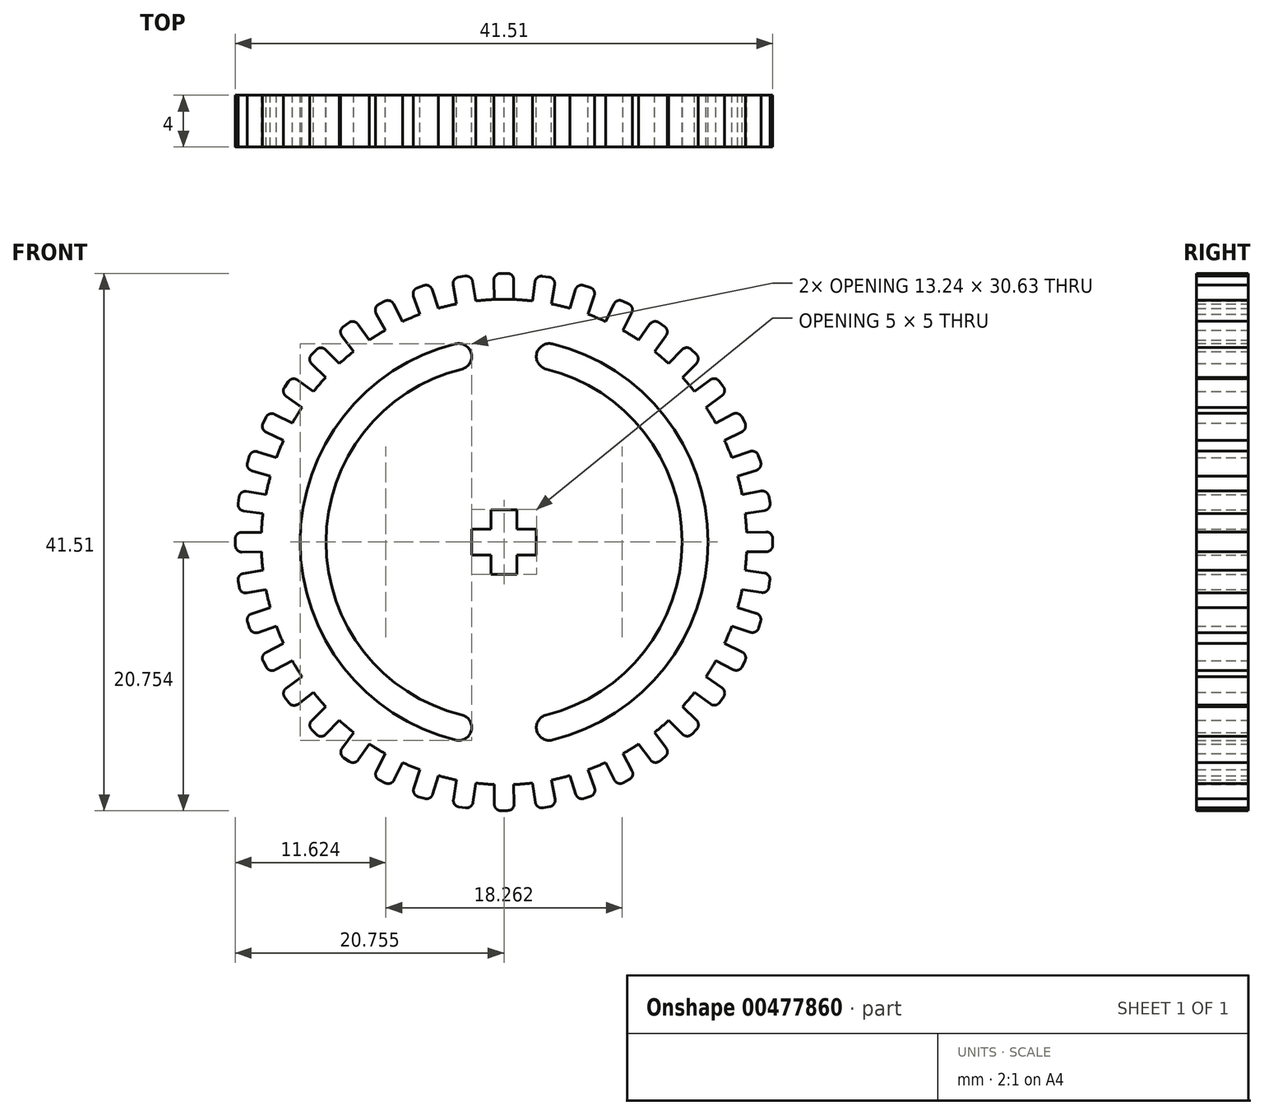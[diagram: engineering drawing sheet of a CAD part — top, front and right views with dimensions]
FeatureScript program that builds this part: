
annotation { "Feature Type Name" : "Feature", "Feature Type Description" : "" }
export const myFeature = defineFeature(function(context is Context, id is Id, definition is map)
    precondition{}
    {
        {
            var Q0;
            Q0=qCreatedBy(makeId("Front.planeOp"),FACE);
            var sketch = newSketch(context, id + "F0", { "sketchPlane" : qUnion([Q0])});
            skCircle(sketch, "E0", {"center": v(-49.28, 19.92) * mm, "radius": 18.75 * mm});
            skLineSegment(sketch, "E1.MirrorCS", {"start": v(-50.28, 22.42) * mm, "end": v(-50.28, 20.92) * mm});
            skLineSegment(sketch, "E2.MirrorCS", {"start": v(-50.28, 20.92) * mm, "end": v(-51.78, 20.92) * mm});
            skArc(sketch, "E3", {"start": v(-46.78, 6.4) * mm, "mid": v(-35.53, 19.92) * mm, "end": v(-46.78, 33.44) * mm});
            skArc(sketch, "E4", {"start": v(-46.78, 4.37) * mm, "mid": v(-33.53, 19.92) * mm, "end": v(-46.78, 35.47) * mm});
            skLineSegment(sketch, "E5", {"start": v(-51.78, 33.44) * mm, "end": v(-51.78, 35.47) * mm});
            skLineSegment(sketch, "E6", {"start": v(-46.78, 33.44) * mm, "end": v(-46.78, 35.47) * mm});
            skLineSegment(sketch, "E7", {"start": v(-51.78, 6.4) * mm, "end": v(-51.78, 4.37) * mm});
            skLineSegment(sketch, "E8", {"start": v(-46.78, 6.4) * mm, "end": v(-46.78, 4.37) * mm});
            skArc(sketch, "E9.trimOffspring", {"start": v(-51.78, 33.44) * mm, "mid": v(-63.03, 19.92) * mm, "end": v(-51.78, 6.4) * mm});
            skArc(sketch, "E10.trimOffspring", {"start": v(-51.78, 35.47) * mm, "mid": v(-65.03, 19.92) * mm, "end": v(-51.78, 4.37) * mm});
            skLineSegment(sketch, "E11", {"start": v(-50.28, 22.42) * mm, "end": v(-48.28, 22.42) * mm});
            skLineSegment(sketch, "E12", {"start": v(-48.28, 17.42) * mm, "end": v(-50.28, 17.42) * mm});
            skLineSegment(sketch, "E13", {"start": v(-50.28, 17.42) * mm, "end": v(-50.28, 18.92) * mm});
            skLineSegment(sketch, "E14", {"start": v(-50.28, 18.92) * mm, "end": v(-51.78, 18.92) * mm});
            skLineSegment(sketch, "E15", {"start": v(-51.78, 18.92) * mm, "end": v(-51.78, 20.92) * mm});
            skPoint(sketch, "E16.startSnap0", {"position": v(-49.28, 22.42) * mm});
            skLineSegment(sketch, "E17", {"start": v(-49.28, 38.67) * mm, "end": v(-48.53, 38.66) * mm});
            skLineSegment(sketch, "E18", {"start": v(-49.28, 38.67) * mm, "end": v(-50.02, 38.66) * mm});
            skPoint(sketch, "E19.center", {"position": v(0, 0) * mm});
            skLineSegment(sketch, "E20", {"start": v(-48.28, 17.42) * mm, "end": v(-48.28, 18.92) * mm});
            skLineSegment(sketch, "E21", {"start": v(-48.28, 18.92) * mm, "end": v(-46.78, 18.92) * mm});
            skLineSegment(sketch, "E22", {"start": v(-46.78, 18.92) * mm, "end": v(-46.78, 20.92) * mm});
            skLineSegment(sketch, "E23", {"start": v(-46.78, 20.92) * mm, "end": v(-48.28, 20.92) * mm});
            skLineSegment(sketch, "E24", {"start": v(-48.28, 20.92) * mm, "end": v(-48.28, 22.42) * mm});
            skLineSegment(sketch, "E25", {"start": v(-50.02, 38.66) * mm, "end": v(-50.05, 40.16) * mm});
            skLineSegment(sketch, "E26", {"start": v(-49.57, 40.67) * mm, "end": v(-49.04, 40.68) * mm});
            skLineSegment(sketch, "E27", {"start": v(-48.53, 40.18) * mm, "end": v(-48.53, 38.66) * mm});
            skPoint(sketch, "E28.visualSharp", {"position": v(-50.06, 40.66) * mm});
            skArc(sketch, "E28.filletArc", {"start": v(-49.57, 40.67) * mm, "mid": v(-49.92, 40.51) * mm, "end": v(-50.05, 40.16) * mm});
            skPoint(sketch, "E29.visualSharp", {"position": v(-48.53, 40.69) * mm});
            skArc(sketch, "E29.filletArc", {"start": v(-48.53, 40.18) * mm, "mid": v(-48.68, 40.54) * mm, "end": v(-49.04, 40.68) * mm});
            skLineSegment(sketch, "E30.1.0", {"start": v(-51.7, 40.05) * mm, "end": v(-51.47, 38.55) * mm});
            skLineSegment(sketch, "E30.1.1", {"start": v(-52.95, 38.31) * mm, "end": v(-53.21, 39.79) * mm});
            skArc(sketch, "E30.1.2", {"start": v(-52.8, 40.37) * mm, "mid": v(-53.13, 40.16) * mm, "end": v(-53.21, 39.79) * mm});
            skLineSegment(sketch, "E30.1.3", {"start": v(-52.8, 40.37) * mm, "end": v(-52.29, 40.46) * mm});
            skArc(sketch, "E30.1.4", {"start": v(-51.7, 40.05) * mm, "mid": v(-51.9, 40.38) * mm, "end": v(-52.29, 40.46) * mm});
            skLineSegment(sketch, "E30.2.0", {"start": v(-54.82, 39.42) * mm, "end": v(-54.35, 37.97) * mm});
            skLineSegment(sketch, "E30.2.1", {"start": v(-55.78, 37.5) * mm, "end": v(-56.27, 38.93) * mm});
            skArc(sketch, "E30.2.2", {"start": v(-55.96, 39.56) * mm, "mid": v(-56.25, 39.3) * mm, "end": v(-56.27, 38.93) * mm});
            skLineSegment(sketch, "E30.2.3", {"start": v(-55.96, 39.56) * mm, "end": v(-55.46, 39.74) * mm});
            skArc(sketch, "E30.2.4", {"start": v(-54.82, 39.42) * mm, "mid": v(-55.07, 39.71) * mm, "end": v(-55.46, 39.74) * mm});
            skLineSegment(sketch, "E30.3.0", {"start": v(-57.8, 38.31) * mm, "end": v(-57.11, 36.96) * mm});
            skLineSegment(sketch, "E30.3.1", {"start": v(-58.45, 36.28) * mm, "end": v(-59.16, 37.6) * mm});
            skArc(sketch, "E30.3.2", {"start": v(-58.95, 38.28) * mm, "mid": v(-59.2, 37.98) * mm, "end": v(-59.16, 37.6) * mm});
            skLineSegment(sketch, "E30.3.3", {"start": v(-58.95, 38.28) * mm, "end": v(-58.48, 38.53) * mm});
            skArc(sketch, "E30.3.4", {"start": v(-57.8, 38.31) * mm, "mid": v(-58.1, 38.56) * mm, "end": v(-58.48, 38.53) * mm});
            skLineSegment(sketch, "E30.4.0", {"start": v(-60.57, 36.75) * mm, "end": v(-59.68, 35.52) * mm});
            skLineSegment(sketch, "E30.4.1", {"start": v(-60.9, 34.64) * mm, "end": v(-61.8, 35.84) * mm});
            skArc(sketch, "E30.4.2", {"start": v(-61.7, 36.54) * mm, "mid": v(-61.9, 36.2) * mm, "end": v(-61.8, 35.84) * mm});
            skLineSegment(sketch, "E30.4.3", {"start": v(-61.7, 36.54) * mm, "end": v(-61.28, 36.86) * mm});
            skArc(sketch, "E30.4.4", {"start": v(-60.57, 36.75) * mm, "mid": v(-60.9, 36.95) * mm, "end": v(-61.28, 36.86) * mm});
            skLineSegment(sketch, "E30.5.0", {"start": v(-63.07, 34.78) * mm, "end": v(-62, 33.7) * mm});
            skLineSegment(sketch, "E30.5.1", {"start": v(-63.05, 32.64) * mm, "end": v(-64.13, 33.68) * mm});
            skArc(sketch, "E30.5.2", {"start": v(-64.15, 34.39) * mm, "mid": v(-64.29, 34.03) * mm, "end": v(-64.13, 33.68) * mm});
            skLineSegment(sketch, "E30.5.3", {"start": v(-64.15, 34.39) * mm, "end": v(-63.78, 34.77) * mm});
            skArc(sketch, "E30.5.4", {"start": v(-63.07, 34.78) * mm, "mid": v(-63.43, 34.92) * mm, "end": v(-63.78, 34.77) * mm});
            skLineSegment(sketch, "E30.6.0", {"start": v(-65.22, 32.44) * mm, "end": v(-64, 31.54) * mm});
            skLineSegment(sketch, "E30.6.1", {"start": v(-64.87, 30.33) * mm, "end": v(-66.1, 31.19) * mm});
            skArc(sketch, "E30.6.2", {"start": v(-66.23, 31.88) * mm, "mid": v(-66.31, 31.5) * mm, "end": v(-66.1, 31.19) * mm});
            skLineSegment(sketch, "E30.6.3", {"start": v(-66.23, 31.88) * mm, "end": v(-65.93, 32.32) * mm});
            skArc(sketch, "E30.6.4", {"start": v(-65.22, 32.44) * mm, "mid": v(-65.6, 32.52) * mm, "end": v(-65.93, 32.32) * mm});
            skLineSegment(sketch, "E30.7.0", {"start": v(-66.98, 29.79) * mm, "end": v(-65.63, 29.1) * mm});
            skLineSegment(sketch, "E30.7.1", {"start": v(-66.3, 27.76) * mm, "end": v(-67.66, 28.42) * mm});
            skArc(sketch, "E30.7.2", {"start": v(-67.9, 29.08) * mm, "mid": v(-67.91, 28.7) * mm, "end": v(-67.66, 28.42) * mm});
            skLineSegment(sketch, "E30.7.3", {"start": v(-67.9, 29.08) * mm, "end": v(-67.66, 29.56) * mm});
            skArc(sketch, "E30.7.4", {"start": v(-66.98, 29.79) * mm, "mid": v(-67.37, 29.82) * mm, "end": v(-67.66, 29.56) * mm});
            skLineSegment(sketch, "E30.8.0", {"start": v(-68.3, 26.9) * mm, "end": v(-66.86, 26.43) * mm});
            skLineSegment(sketch, "E30.8.1", {"start": v(-67.32, 25) * mm, "end": v(-68.76, 25.43) * mm});
            skArc(sketch, "E30.8.2", {"start": v(-69.1, 26.06) * mm, "mid": v(-69.06, 25.68) * mm, "end": v(-68.76, 25.43) * mm});
            skLineSegment(sketch, "E30.8.3", {"start": v(-69.1, 26.06) * mm, "end": v(-68.94, 26.57) * mm});
            skArc(sketch, "E30.8.4", {"start": v(-68.3, 26.9) * mm, "mid": v(-68.7, 26.86) * mm, "end": v(-68.94, 26.57) * mm});
            skLineSegment(sketch, "E30.9.0", {"start": v(-69.16, 23.83) * mm, "end": v(-67.66, 23.6) * mm});
            skLineSegment(sketch, "E30.9.1", {"start": v(-67.9, 22.11) * mm, "end": v(-69.38, 22.32) * mm});
            skArc(sketch, "E30.9.2", {"start": v(-69.8, 22.88) * mm, "mid": v(-69.71, 22.51) * mm, "end": v(-69.38, 22.32) * mm});
            skLineSegment(sketch, "E30.9.3", {"start": v(-69.8, 22.88) * mm, "end": v(-69.74, 23.4) * mm});
            skArc(sketch, "E30.9.4", {"start": v(-69.16, 23.83) * mm, "mid": v(-69.54, 23.74) * mm, "end": v(-69.74, 23.4) * mm});
            skLineSegment(sketch, "E30.10.0", {"start": v(-69.53, 20.67) * mm, "end": v(-68.01, 20.67) * mm});
            skLineSegment(sketch, "E30.10.1", {"start": v(-68.01, 19.17) * mm, "end": v(-69.5, 19.14) * mm});
            skArc(sketch, "E30.10.2", {"start": v(-70.02, 19.63) * mm, "mid": v(-69.87, 19.28) * mm, "end": v(-69.5, 19.14) * mm});
            skLineSegment(sketch, "E30.10.3", {"start": v(-70.02, 19.63) * mm, "end": v(-70.03, 20.16) * mm});
            skArc(sketch, "E30.10.4", {"start": v(-69.53, 20.67) * mm, "mid": v(-69.89, 20.52) * mm, "end": v(-70.03, 20.16) * mm});
            skLineSegment(sketch, "E30.11.0", {"start": v(-69.4, 17.5) * mm, "end": v(-67.9, 17.73) * mm});
            skLineSegment(sketch, "E30.11.1", {"start": v(-67.66, 16.25) * mm, "end": v(-69.14, 15.99) * mm});
            skArc(sketch, "E30.11.2", {"start": v(-69.72, 16.4) * mm, "mid": v(-69.51, 16.07) * mm, "end": v(-69.14, 15.99) * mm});
            skLineSegment(sketch, "E30.11.3", {"start": v(-69.72, 16.4) * mm, "end": v(-69.81, 16.91) * mm});
            skArc(sketch, "E30.11.4", {"start": v(-69.4, 17.5) * mm, "mid": v(-69.73, 17.3) * mm, "end": v(-69.81, 16.91) * mm});
            skLineSegment(sketch, "E30.12.0", {"start": v(-68.77, 14.38) * mm, "end": v(-67.32, 14.85) * mm});
            skLineSegment(sketch, "E30.12.1", {"start": v(-66.86, 13.42) * mm, "end": v(-68.28, 12.93) * mm});
            skArc(sketch, "E30.12.2", {"start": v(-68.91, 13.24) * mm, "mid": v(-68.66, 12.95) * mm, "end": v(-68.28, 12.93) * mm});
            skLineSegment(sketch, "E30.12.3", {"start": v(-68.91, 13.24) * mm, "end": v(-69.09, 13.74) * mm});
            skArc(sketch, "E30.12.4", {"start": v(-68.77, 14.38) * mm, "mid": v(-69.06, 14.12) * mm, "end": v(-69.09, 13.74) * mm});
            skLineSegment(sketch, "E30.13.0", {"start": v(-67.66, 11.4) * mm, "end": v(-66.3, 12.09) * mm});
            skLineSegment(sketch, "E30.13.1", {"start": v(-65.63, 10.75) * mm, "end": v(-66.95, 10.04) * mm});
            skArc(sketch, "E30.13.2", {"start": v(-67.63, 10.25) * mm, "mid": v(-67.33, 10) * mm, "end": v(-66.95, 10.04) * mm});
            skLineSegment(sketch, "E30.13.3", {"start": v(-67.63, 10.25) * mm, "end": v(-67.88, 10.71) * mm});
            skArc(sketch, "E30.13.4", {"start": v(-67.66, 11.4) * mm, "mid": v(-67.91, 11.1) * mm, "end": v(-67.88, 10.71) * mm});
            skLineSegment(sketch, "E30.14.0", {"start": v(-66.1, 8.62) * mm, "end": v(-64.87, 9.52) * mm});
            skLineSegment(sketch, "E30.14.1", {"start": v(-64, 8.3) * mm, "end": v(-65.19, 7.4) * mm});
            skArc(sketch, "E30.14.2", {"start": v(-65.89, 7.5) * mm, "mid": v(-65.56, 7.3) * mm, "end": v(-65.19, 7.4) * mm});
            skLineSegment(sketch, "E30.14.3", {"start": v(-65.89, 7.5) * mm, "end": v(-66.2, 7.92) * mm});
            skArc(sketch, "E30.14.4", {"start": v(-66.1, 8.62) * mm, "mid": v(-66.3, 8.3) * mm, "end": v(-66.2, 7.92) * mm});
            skLineSegment(sketch, "E30.15.0", {"start": v(-64.13, 6.13) * mm, "end": v(-63.05, 7.2) * mm});
            skLineSegment(sketch, "E30.15.1", {"start": v(-62, 6.15) * mm, "end": v(-63.03, 5.06) * mm});
            skArc(sketch, "E30.15.2", {"start": v(-63.74, 5.05) * mm, "mid": v(-63.38, 4.91) * mm, "end": v(-63.03, 5.06) * mm});
            skLineSegment(sketch, "E30.15.3", {"start": v(-63.74, 5.05) * mm, "end": v(-64.12, 5.42) * mm});
            skArc(sketch, "E30.15.4", {"start": v(-64.13, 6.13) * mm, "mid": v(-64.27, 5.77) * mm, "end": v(-64.12, 5.42) * mm});
            skLineSegment(sketch, "E30.16.0", {"start": v(-61.79, 3.98) * mm, "end": v(-60.9, 5.2) * mm});
            skLineSegment(sketch, "E30.16.1", {"start": v(-59.68, 4.33) * mm, "end": v(-60.54, 3.1) * mm});
            skArc(sketch, "E30.16.2", {"start": v(-61.23, 2.97) * mm, "mid": v(-60.86, 2.89) * mm, "end": v(-60.54, 3.1) * mm});
            skLineSegment(sketch, "E30.16.3", {"start": v(-61.23, 2.97) * mm, "end": v(-61.67, 3.27) * mm});
            skArc(sketch, "E30.16.4", {"start": v(-61.79, 3.98) * mm, "mid": v(-61.88, 3.6) * mm, "end": v(-61.67, 3.27) * mm});
            skLineSegment(sketch, "E30.17.0", {"start": v(-59.14, 2.22) * mm, "end": v(-58.45, 3.57) * mm});
            skLineSegment(sketch, "E30.17.1", {"start": v(-57.11, 2.9) * mm, "end": v(-57.77, 1.54) * mm});
            skArc(sketch, "E30.17.2", {"start": v(-58.43, 1.3) * mm, "mid": v(-58.05, 1.29) * mm, "end": v(-57.77, 1.54) * mm});
            skLineSegment(sketch, "E30.17.3", {"start": v(-58.43, 1.3) * mm, "end": v(-58.91, 1.54) * mm});
            skArc(sketch, "E30.17.4", {"start": v(-59.14, 2.22) * mm, "mid": v(-59.17, 1.83) * mm, "end": v(-58.91, 1.54) * mm});
            skLineSegment(sketch, "E30.18.0", {"start": v(-56.25, 0.9) * mm, "end": v(-55.78, 2.34) * mm});
            skLineSegment(sketch, "E30.18.1", {"start": v(-54.35, 1.87) * mm, "end": v(-54.79, 0.44) * mm});
            skArc(sketch, "E30.18.2", {"start": v(-55.4, 0.1) * mm, "mid": v(-55.03, 0.14) * mm, "end": v(-54.79, 0.44) * mm});
            skLineSegment(sketch, "E30.18.3", {"start": v(-55.4, 0.1) * mm, "end": v(-55.92, 0.26) * mm});
            skArc(sketch, "E30.18.4", {"start": v(-56.25, 0.9) * mm, "mid": v(-56.22, 0.5) * mm, "end": v(-55.92, 0.26) * mm});
            skLineSegment(sketch, "E30.19.0", {"start": v(-53.18, 0.03) * mm, "end": v(-52.95, 1.54) * mm});
            skLineSegment(sketch, "E30.19.1", {"start": v(-51.47, 1.3) * mm, "end": v(-51.67, -0.18) * mm});
            skArc(sketch, "E30.19.2", {"start": v(-52.23, -0.61) * mm, "mid": v(-51.86, -0.51) * mm, "end": v(-51.67, -0.18) * mm});
            skLineSegment(sketch, "E30.19.3", {"start": v(-52.23, -0.61) * mm, "end": v(-52.76, -0.54) * mm});
            skArc(sketch, "E30.19.4", {"start": v(-53.18, 0.03) * mm, "mid": v(-53.1, -0.34) * mm, "end": v(-52.76, -0.54) * mm});
            skLineSegment(sketch, "E30.20.0", {"start": v(-50.02, -0.33) * mm, "end": v(-50.02, 1.19) * mm});
            skLineSegment(sketch, "E30.20.1", {"start": v(-48.53, 1.19) * mm, "end": v(-48.5, -0.31) * mm});
            skArc(sketch, "E30.20.2", {"start": v(-48.99, -0.82) * mm, "mid": v(-48.63, -0.67) * mm, "end": v(-48.5, -0.31) * mm});
            skLineSegment(sketch, "E30.20.3", {"start": v(-48.99, -0.82) * mm, "end": v(-49.51, -0.83) * mm});
            skArc(sketch, "E30.20.4", {"start": v(-50.02, -0.33) * mm, "mid": v(-49.87, -0.69) * mm, "end": v(-49.51, -0.83) * mm});
            skLineSegment(sketch, "E30.21.0", {"start": v(-46.85, -0.2) * mm, "end": v(-47.08, 1.3) * mm});
            skLineSegment(sketch, "E30.21.1", {"start": v(-45.6, 1.54) * mm, "end": v(-45.34, 0.06) * mm});
            skArc(sketch, "E30.21.2", {"start": v(-45.74, -0.52) * mm, "mid": v(-45.42, -0.31) * mm, "end": v(-45.34, 0.06) * mm});
            skLineSegment(sketch, "E30.21.3", {"start": v(-45.74, -0.52) * mm, "end": v(-46.27, -0.61) * mm});
            skArc(sketch, "E30.21.4", {"start": v(-46.85, -0.2) * mm, "mid": v(-46.64, -0.53) * mm, "end": v(-46.27, -0.61) * mm});
            skLineSegment(sketch, "E30.22.0", {"start": v(-43.73, 0.43) * mm, "end": v(-44.2, 1.87) * mm});
            skLineSegment(sketch, "E30.22.1", {"start": v(-42.77, 2.34) * mm, "end": v(-42.28, 0.92) * mm});
            skArc(sketch, "E30.22.2", {"start": v(-42.59, 0.28) * mm, "mid": v(-42.3, 0.54) * mm, "end": v(-42.28, 0.92) * mm});
            skLineSegment(sketch, "E30.22.3", {"start": v(-42.59, 0.28) * mm, "end": v(-43.09, 0.11) * mm});
            skArc(sketch, "E30.22.4", {"start": v(-43.73, 0.43) * mm, "mid": v(-43.48, 0.13) * mm, "end": v(-43.09, 0.11) * mm});
            skLineSegment(sketch, "E30.23.0", {"start": v(-40.75, 1.54) * mm, "end": v(-41.44, 2.9) * mm});
            skLineSegment(sketch, "E30.23.1", {"start": v(-40.1, 3.57) * mm, "end": v(-39.4, 2.25) * mm});
            skArc(sketch, "E30.23.2", {"start": v(-39.6, 1.57) * mm, "mid": v(-39.36, 1.87) * mm, "end": v(-39.4, 2.25) * mm});
            skLineSegment(sketch, "E30.23.3", {"start": v(-39.6, 1.57) * mm, "end": v(-40.07, 1.32) * mm});
            skArc(sketch, "E30.23.4", {"start": v(-40.75, 1.54) * mm, "mid": v(-40.45, 1.29) * mm, "end": v(-40.07, 1.32) * mm});
            skLineSegment(sketch, "E30.24.0", {"start": v(-37.98, 3.1) * mm, "end": v(-38.87, 4.33) * mm});
            skLineSegment(sketch, "E30.24.1", {"start": v(-37.66, 5.2) * mm, "end": v(-36.75, 4.01) * mm});
            skArc(sketch, "E30.24.2", {"start": v(-36.85, 3.31) * mm, "mid": v(-36.65, 3.64) * mm, "end": v(-36.75, 4.01) * mm});
            skLineSegment(sketch, "E30.24.3", {"start": v(-36.85, 3.31) * mm, "end": v(-37.27, 3) * mm});
            skArc(sketch, "E30.24.4", {"start": v(-37.98, 3.1) * mm, "mid": v(-37.64, 2.9) * mm, "end": v(-37.27, 3) * mm});
            skLineSegment(sketch, "E30.25.0", {"start": v(-35.48, 5.07) * mm, "end": v(-36.56, 6.15) * mm});
            skLineSegment(sketch, "E30.25.1", {"start": v(-35.5, 7.2) * mm, "end": v(-34.42, 6.17) * mm});
            skArc(sketch, "E30.25.2", {"start": v(-34.4, 5.46) * mm, "mid": v(-34.26, 5.82) * mm, "end": v(-34.42, 6.17) * mm});
            skLineSegment(sketch, "E30.25.3", {"start": v(-34.4, 5.46) * mm, "end": v(-34.77, 5.08) * mm});
            skArc(sketch, "E30.25.4", {"start": v(-35.48, 5.07) * mm, "mid": v(-35.12, 4.92) * mm, "end": v(-34.77, 5.08) * mm});
            skLineSegment(sketch, "E30.26.0", {"start": v(-33.33, 7.41) * mm, "end": v(-34.56, 8.3) * mm});
            skLineSegment(sketch, "E30.26.1", {"start": v(-33.68, 9.52) * mm, "end": v(-32.45, 8.66) * mm});
            skArc(sketch, "E30.26.2", {"start": v(-32.32, 7.96) * mm, "mid": v(-32.24, 8.34) * mm, "end": v(-32.45, 8.66) * mm});
            skLineSegment(sketch, "E30.26.3", {"start": v(-32.32, 7.96) * mm, "end": v(-32.62, 7.53) * mm});
            skArc(sketch, "E30.26.4", {"start": v(-33.33, 7.41) * mm, "mid": v(-32.95, 7.32) * mm, "end": v(-32.62, 7.53) * mm});
            skLineSegment(sketch, "E30.27.0", {"start": v(-31.57, 10.06) * mm, "end": v(-32.92, 10.75) * mm});
            skLineSegment(sketch, "E30.27.1", {"start": v(-32.24, 12.09) * mm, "end": v(-30.9, 11.43) * mm});
            skArc(sketch, "E30.27.2", {"start": v(-30.66, 10.76) * mm, "mid": v(-30.64, 11.15) * mm, "end": v(-30.9, 11.43) * mm});
            skLineSegment(sketch, "E30.27.3", {"start": v(-30.66, 10.76) * mm, "end": v(-30.9, 10.29) * mm});
            skArc(sketch, "E30.27.4", {"start": v(-31.57, 10.06) * mm, "mid": v(-31.18, 10.03) * mm, "end": v(-30.9, 10.29) * mm});
            skLineSegment(sketch, "E30.28.0", {"start": v(-30.24, 12.95) * mm, "end": v(-31.69, 13.42) * mm});
            skLineSegment(sketch, "E30.28.1", {"start": v(-31.23, 14.85) * mm, "end": v(-29.79, 14.41) * mm});
            skArc(sketch, "E30.28.2", {"start": v(-29.46, 13.79) * mm, "mid": v(-29.5, 14.17) * mm, "end": v(-29.79, 14.41) * mm});
            skLineSegment(sketch, "E30.28.3", {"start": v(-29.46, 13.79) * mm, "end": v(-29.6, 13.28) * mm});
            skArc(sketch, "E30.28.4", {"start": v(-30.24, 12.95) * mm, "mid": v(-29.86, 12.98) * mm, "end": v(-29.6, 13.28) * mm});
            skLineSegment(sketch, "E30.29.0", {"start": v(-29.39, 16.01) * mm, "end": v(-30.89, 16.25) * mm});
            skLineSegment(sketch, "E30.29.1", {"start": v(-30.65, 17.73) * mm, "end": v(-29.17, 17.53) * mm});
            skArc(sketch, "E30.29.2", {"start": v(-28.74, 16.96) * mm, "mid": v(-28.84, 17.34) * mm, "end": v(-29.17, 17.53) * mm});
            skLineSegment(sketch, "E30.29.3", {"start": v(-28.74, 16.96) * mm, "end": v(-28.81, 16.44) * mm});
            skArc(sketch, "E30.29.4", {"start": v(-29.39, 16.01) * mm, "mid": v(-29.01, 16.1) * mm, "end": v(-28.81, 16.44) * mm});
            skLineSegment(sketch, "E30.30.0", {"start": v(-29.02, 19.17) * mm, "end": v(-30.54, 19.17) * mm});
            skLineSegment(sketch, "E30.30.1", {"start": v(-30.54, 20.67) * mm, "end": v(-29.04, 20.7) * mm});
            skArc(sketch, "E30.30.2", {"start": v(-28.53, 20.21) * mm, "mid": v(-28.68, 20.56) * mm, "end": v(-29.04, 20.7) * mm});
            skLineSegment(sketch, "E30.30.3", {"start": v(-28.53, 20.21) * mm, "end": v(-28.52, 19.68) * mm});
            skArc(sketch, "E30.30.4", {"start": v(-29.02, 19.17) * mm, "mid": v(-28.66, 19.32) * mm, "end": v(-28.52, 19.68) * mm});
            skLineSegment(sketch, "E30.31.0", {"start": v(-29.15, 22.35) * mm, "end": v(-30.65, 22.11) * mm});
            skLineSegment(sketch, "E30.31.1", {"start": v(-30.89, 23.6) * mm, "end": v(-29.41, 23.86) * mm});
            skArc(sketch, "E30.31.2", {"start": v(-28.83, 23.46) * mm, "mid": v(-29.04, 23.78) * mm, "end": v(-29.41, 23.86) * mm});
            skLineSegment(sketch, "E30.31.3", {"start": v(-28.83, 23.46) * mm, "end": v(-28.74, 22.93) * mm});
            skArc(sketch, "E30.31.4", {"start": v(-29.15, 22.35) * mm, "mid": v(-28.82, 22.56) * mm, "end": v(-28.74, 22.93) * mm});
            skLineSegment(sketch, "E30.32.0", {"start": v(-29.78, 25.47) * mm, "end": v(-31.23, 25) * mm});
            skLineSegment(sketch, "E30.32.1", {"start": v(-31.69, 26.43) * mm, "end": v(-30.27, 26.92) * mm});
            skArc(sketch, "E30.32.2", {"start": v(-29.64, 26.6) * mm, "mid": v(-29.89, 26.9) * mm, "end": v(-30.27, 26.92) * mm});
            skLineSegment(sketch, "E30.32.3", {"start": v(-29.64, 26.6) * mm, "end": v(-29.46, 26.1) * mm});
            skArc(sketch, "E30.32.4", {"start": v(-29.78, 25.47) * mm, "mid": v(-29.49, 25.72) * mm, "end": v(-29.46, 26.1) * mm});
            skLineSegment(sketch, "E30.33.0", {"start": v(-30.89, 28.45) * mm, "end": v(-32.24, 27.76) * mm});
            skLineSegment(sketch, "E30.33.1", {"start": v(-32.92, 29.1) * mm, "end": v(-31.6, 29.8) * mm});
            skArc(sketch, "E30.33.2", {"start": v(-30.92, 29.6) * mm, "mid": v(-31.22, 29.84) * mm, "end": v(-31.6, 29.8) * mm});
            skLineSegment(sketch, "E30.33.3", {"start": v(-30.92, 29.6) * mm, "end": v(-30.67, 29.13) * mm});
            skArc(sketch, "E30.33.4", {"start": v(-30.89, 28.45) * mm, "mid": v(-30.64, 28.75) * mm, "end": v(-30.67, 29.13) * mm});
            skLineSegment(sketch, "E30.34.0", {"start": v(-32.45, 31.22) * mm, "end": v(-33.68, 30.33) * mm});
            skLineSegment(sketch, "E30.34.1", {"start": v(-34.56, 31.54) * mm, "end": v(-33.36, 32.45) * mm});
            skArc(sketch, "E30.34.2", {"start": v(-32.66, 32.35) * mm, "mid": v(-33, 32.54) * mm, "end": v(-33.36, 32.45) * mm});
            skLineSegment(sketch, "E30.34.3", {"start": v(-32.66, 32.35) * mm, "end": v(-32.34, 31.93) * mm});
            skArc(sketch, "E30.34.4", {"start": v(-32.45, 31.22) * mm, "mid": v(-32.25, 31.55) * mm, "end": v(-32.34, 31.93) * mm});
            skLineSegment(sketch, "E30.35.0", {"start": v(-34.42, 33.72) * mm, "end": v(-35.5, 32.64) * mm});
            skLineSegment(sketch, "E30.35.1", {"start": v(-36.56, 33.7) * mm, "end": v(-35.52, 34.78) * mm});
            skArc(sketch, "E30.35.2", {"start": v(-34.81, 34.8) * mm, "mid": v(-35.17, 34.94) * mm, "end": v(-35.52, 34.78) * mm});
            skLineSegment(sketch, "E30.35.3", {"start": v(-34.81, 34.8) * mm, "end": v(-34.43, 34.43) * mm});
            skArc(sketch, "E30.35.4", {"start": v(-34.42, 33.72) * mm, "mid": v(-34.28, 34.07) * mm, "end": v(-34.43, 34.43) * mm});
            skLineSegment(sketch, "E30.36.0", {"start": v(-36.76, 35.87) * mm, "end": v(-37.66, 34.64) * mm});
            skLineSegment(sketch, "E30.36.1", {"start": v(-38.87, 35.52) * mm, "end": v(-38.01, 36.75) * mm});
            skArc(sketch, "E30.36.2", {"start": v(-37.32, 36.88) * mm, "mid": v(-37.7, 36.96) * mm, "end": v(-38.01, 36.75) * mm});
            skLineSegment(sketch, "E30.36.3", {"start": v(-37.32, 36.88) * mm, "end": v(-36.88, 36.57) * mm});
            skArc(sketch, "E30.36.4", {"start": v(-36.76, 35.87) * mm, "mid": v(-36.67, 36.25) * mm, "end": v(-36.88, 36.57) * mm});
            skLineSegment(sketch, "E30.37.0", {"start": v(-39.41, 37.63) * mm, "end": v(-40.1, 36.28) * mm});
            skLineSegment(sketch, "E30.37.1", {"start": v(-41.44, 36.96) * mm, "end": v(-40.78, 38.3) * mm});
            skArc(sketch, "E30.37.2", {"start": v(-40.12, 38.54) * mm, "mid": v(-40.5, 38.56) * mm, "end": v(-40.78, 38.3) * mm});
            skLineSegment(sketch, "E30.37.3", {"start": v(-40.12, 38.54) * mm, "end": v(-39.64, 38.3) * mm});
            skArc(sketch, "E30.37.4", {"start": v(-39.41, 37.63) * mm, "mid": v(-39.38, 38.02) * mm, "end": v(-39.64, 38.3) * mm});
            skLineSegment(sketch, "E30.38.0", {"start": v(-42.3, 38.96) * mm, "end": v(-42.77, 37.5) * mm});
            skLineSegment(sketch, "E30.38.1", {"start": v(-44.2, 37.97) * mm, "end": v(-43.76, 39.4) * mm});
            skArc(sketch, "E30.38.2", {"start": v(-43.14, 39.74) * mm, "mid": v(-43.52, 39.7) * mm, "end": v(-43.76, 39.4) * mm});
            skLineSegment(sketch, "E30.38.3", {"start": v(-43.14, 39.74) * mm, "end": v(-42.63, 39.59) * mm});
            skArc(sketch, "E30.38.4", {"start": v(-42.3, 38.96) * mm, "mid": v(-42.34, 39.34) * mm, "end": v(-42.63, 39.59) * mm});
            skLineSegment(sketch, "E30.39.0", {"start": v(-45.37, 39.81) * mm, "end": v(-45.6, 38.31) * mm});
            skLineSegment(sketch, "E30.39.1", {"start": v(-47.08, 38.55) * mm, "end": v(-46.88, 40.03) * mm});
            skArc(sketch, "E30.39.2", {"start": v(-46.32, 40.46) * mm, "mid": v(-46.69, 40.36) * mm, "end": v(-46.88, 40.03) * mm});
            skLineSegment(sketch, "E30.39.3", {"start": v(-46.32, 40.46) * mm, "end": v(-45.8, 40.39) * mm});
            skArc(sketch, "E30.39.4", {"start": v(-45.37, 39.81) * mm, "mid": v(-45.46, 40.19) * mm, "end": v(-45.8, 40.39) * mm});
            skSolve(sketch);
        }
        {
            var Q0;
            Q0=makeQuery(id+"F0.imprint","IMPRINT",FACE,{"disambiguationData":[TD([[makeQuery(id+"F0.imprint","IMPRINT",EDGE,{"derivedFrom":sQuery(id+"F0.wireOp",EDGE,"E3")}),1.0]])]});
            extrude(context, id + "F1", {"entities" : qUnion([Q0]), "depth" : 4 * mm, "offsetDistance" : 25 * mm});
        }
        {
            var Q0;
            Q0=makeQuery(id+"F1.opExtrude","SWEPT_EDGE",EDGE,{"disambiguationData":[OSD([sQuery(id+"F0.wireOp",EDGE,"E5"),sQuery(id+"F0.wireOp",EDGE,"E10.trimOffspring")])]});
            var Q1;
            Q1=makeQuery(id+"F1.opExtrude","SWEPT_EDGE",EDGE,{"disambiguationData":[OSD([sQuery(id+"F0.wireOp",EDGE,"E5"),sQuery(id+"F0.wireOp",EDGE,"E9.trimOffspring")])]});
            var Q2;
            Q2=makeQuery(id+"F1.opExtrude","SWEPT_EDGE",EDGE,{"disambiguationData":[OSD([sQuery(id+"F0.wireOp",EDGE,"E7"),sQuery(id+"F0.wireOp",EDGE,"E10.trimOffspring")])]});
            var Q3;
            Q3=makeQuery(id+"F1.opExtrude","SWEPT_EDGE",EDGE,{"disambiguationData":[OSD([sQuery(id+"F0.wireOp",EDGE,"E7"),sQuery(id+"F0.wireOp",EDGE,"E9.trimOffspring")])]});
            var Q4;
            Q4=makeQuery(id+"F1.opExtrude","SWEPT_EDGE",EDGE,{"disambiguationData":[OSD([sQuery(id+"F0.wireOp",EDGE,"E3"),sQuery(id+"F0.wireOp",EDGE,"E8")])]});
            var Q5;
            Q5=makeQuery(id+"F1.opExtrude","SWEPT_EDGE",EDGE,{"disambiguationData":[OSD([sQuery(id+"F0.wireOp",EDGE,"E4"),sQuery(id+"F0.wireOp",EDGE,"E8")])]});
            var Q6;
            Q6=makeQuery(id+"F1.opExtrude","SWEPT_EDGE",EDGE,{"disambiguationData":[OSD([sQuery(id+"F0.wireOp",EDGE,"E4"),sQuery(id+"F0.wireOp",EDGE,"E6")])]});
            var Q7;
            Q7=makeQuery(id+"F1.opExtrude","SWEPT_EDGE",EDGE,{"disambiguationData":[OSD([sQuery(id+"F0.wireOp",EDGE,"E3"),sQuery(id+"F0.wireOp",EDGE,"E6")])]});
            fillet(context, id + "F2", {"entities" : qUnion([Q0, Q1, Q2, Q3, Q4, Q5, Q6, Q7]), "radius" : 1 * mm, "tangentPropagation" : true, "allowEdgeOverflow" : false});
        }
        {
            var Q0;
            {var subQ0=sQuery(id+"F0.wireOp",EDGE,"E30.2.0");Q0=makeQuery(id+"F0.imprint","IMPRINT",FACE,{"disambiguationData":[TD([[makeQuery(id+"F0.imprint","IMPRINT",EDGE,{"derivedFrom":subQ0}),-1.0]])]});}
            var Q1;
            {var subQ0=sQuery(id+"F0.wireOp",EDGE,"E30.1.0");Q1=makeQuery(id+"F0.imprint","IMPRINT",FACE,{"disambiguationData":[TD([[makeQuery(id+"F0.imprint","IMPRINT",EDGE,{"derivedFrom":subQ0}),-1.0]])]});}
            var Q2;
            {var subQ0=sQuery(id+"F0.wireOp",EDGE,"E25");Q2=makeQuery(id+"F0.imprint","IMPRINT",FACE,{"disambiguationData":[TD([[makeQuery(id+"F0.imprint","IMPRINT",EDGE,{"derivedFrom":subQ0}),-1.0]])]});}
            var Q3;
            {var subQ1=sQuery(id+"F0.wireOp",EDGE,"E30.39.0");Q3=makeQuery(id+"F0.imprint","IMPRINT",FACE,{"disambiguationData":[TD([[makeQuery(id+"F0.imprint","IMPRINT",EDGE,{"derivedFrom":subQ1}),-1.0]])]});}
            var Q4;
            {var subQ1=sQuery(id+"F0.wireOp",EDGE,"E30.38.0");Q4=makeQuery(id+"F0.imprint","IMPRINT",FACE,{"disambiguationData":[TD([[makeQuery(id+"F0.imprint","IMPRINT",EDGE,{"derivedFrom":subQ1}),-1.0]])]});}
            var Q5;
            {var subQ1=sQuery(id+"F0.wireOp",EDGE,"E30.37.0");Q5=makeQuery(id+"F0.imprint","IMPRINT",FACE,{"disambiguationData":[TD([[makeQuery(id+"F0.imprint","IMPRINT",EDGE,{"derivedFrom":subQ1}),-1.0]])]});}
            var Q6;
            {var subQ1=sQuery(id+"F0.wireOp",EDGE,"E30.36.0");Q6=makeQuery(id+"F0.imprint","IMPRINT",FACE,{"disambiguationData":[TD([[makeQuery(id+"F0.imprint","IMPRINT",EDGE,{"derivedFrom":subQ1}),-1.0]])]});}
            var Q7;
            {var subQ0=sQuery(id+"F0.wireOp",EDGE,"E30.35.0");Q7=makeQuery(id+"F0.imprint","IMPRINT",FACE,{"disambiguationData":[TD([[makeQuery(id+"F0.imprint","IMPRINT",EDGE,{"derivedFrom":subQ0}),-1.0]])]});}
            var Q8;
            {var subQ1=sQuery(id+"F0.wireOp",EDGE,"E30.34.0");Q8=makeQuery(id+"F0.imprint","IMPRINT",FACE,{"disambiguationData":[TD([[makeQuery(id+"F0.imprint","IMPRINT",EDGE,{"derivedFrom":subQ1}),-1.0]])]});}
            var Q9;
            {var subQ1=sQuery(id+"F0.wireOp",EDGE,"E30.33.0");Q9=makeQuery(id+"F0.imprint","IMPRINT",FACE,{"disambiguationData":[TD([[makeQuery(id+"F0.imprint","IMPRINT",EDGE,{"derivedFrom":subQ1}),-1.0]])]});}
            var Q10;
            {var subQ1=sQuery(id+"F0.wireOp",EDGE,"E30.32.0");Q10=makeQuery(id+"F0.imprint","IMPRINT",FACE,{"disambiguationData":[TD([[makeQuery(id+"F0.imprint","IMPRINT",EDGE,{"derivedFrom":subQ1}),-1.0]])]});}
            var Q11;
            {var subQ1=sQuery(id+"F0.wireOp",EDGE,"E30.31.0");Q11=makeQuery(id+"F0.imprint","IMPRINT",FACE,{"disambiguationData":[TD([[makeQuery(id+"F0.imprint","IMPRINT",EDGE,{"derivedFrom":subQ1}),-1.0]])]});}
            var Q12;
            {var subQ1=sQuery(id+"F0.wireOp",EDGE,"E30.30.0");Q12=makeQuery(id+"F0.imprint","IMPRINT",FACE,{"disambiguationData":[TD([[makeQuery(id+"F0.imprint","IMPRINT",EDGE,{"derivedFrom":subQ1}),-1.0]])]});}
            var Q13;
            {var subQ1=sQuery(id+"F0.wireOp",EDGE,"E30.3.0");Q13=makeQuery(id+"F0.imprint","IMPRINT",FACE,{"disambiguationData":[TD([[makeQuery(id+"F0.imprint","IMPRINT",EDGE,{"derivedFrom":subQ1}),-1.0]])]});}
            var Q14;
            {var subQ1=sQuery(id+"F0.wireOp",EDGE,"E30.4.0");Q14=makeQuery(id+"F0.imprint","IMPRINT",FACE,{"disambiguationData":[TD([[makeQuery(id+"F0.imprint","IMPRINT",EDGE,{"derivedFrom":subQ1}),-1.0]])]});}
            var Q15;
            {var subQ1=sQuery(id+"F0.wireOp",EDGE,"E30.5.0");Q15=makeQuery(id+"F0.imprint","IMPRINT",FACE,{"disambiguationData":[TD([[makeQuery(id+"F0.imprint","IMPRINT",EDGE,{"derivedFrom":subQ1}),-1.0]])]});}
            var Q16;
            {var subQ1=sQuery(id+"F0.wireOp",EDGE,"E30.6.0");Q16=makeQuery(id+"F0.imprint","IMPRINT",FACE,{"disambiguationData":[TD([[makeQuery(id+"F0.imprint","IMPRINT",EDGE,{"derivedFrom":subQ1}),-1.0]])]});}
            var Q17;
            {var subQ0=sQuery(id+"F0.wireOp",EDGE,"E30.7.0");Q17=makeQuery(id+"F0.imprint","IMPRINT",FACE,{"disambiguationData":[TD([[makeQuery(id+"F0.imprint","IMPRINT",EDGE,{"derivedFrom":subQ0}),-1.0]])]});}
            var Q18;
            {var subQ1=sQuery(id+"F0.wireOp",EDGE,"E30.8.0");Q18=makeQuery(id+"F0.imprint","IMPRINT",FACE,{"disambiguationData":[TD([[makeQuery(id+"F0.imprint","IMPRINT",EDGE,{"derivedFrom":subQ1}),-1.0]])]});}
            var Q19;
            {var subQ1=sQuery(id+"F0.wireOp",EDGE,"E30.9.0");Q19=makeQuery(id+"F0.imprint","IMPRINT",FACE,{"disambiguationData":[TD([[makeQuery(id+"F0.imprint","IMPRINT",EDGE,{"derivedFrom":subQ1}),-1.0]])]});}
            var Q20;
            {var subQ1=sQuery(id+"F0.wireOp",EDGE,"E30.11.0");Q20=makeQuery(id+"F0.imprint","IMPRINT",FACE,{"disambiguationData":[TD([[makeQuery(id+"F0.imprint","IMPRINT",EDGE,{"derivedFrom":subQ1}),-1.0]])]});}
            var Q21;
            {var subQ0=sQuery(id+"F0.wireOp",EDGE,"E30.12.0");Q21=makeQuery(id+"F0.imprint","IMPRINT",FACE,{"disambiguationData":[TD([[makeQuery(id+"F0.imprint","IMPRINT",EDGE,{"derivedFrom":subQ0}),-1.0]])]});}
            var Q22;
            {var subQ1=sQuery(id+"F0.wireOp",EDGE,"E30.13.0");Q22=makeQuery(id+"F0.imprint","IMPRINT",FACE,{"disambiguationData":[TD([[makeQuery(id+"F0.imprint","IMPRINT",EDGE,{"derivedFrom":subQ1}),-1.0]])]});}
            var Q23;
            {var subQ1=sQuery(id+"F0.wireOp",EDGE,"E30.10.0");Q23=makeQuery(id+"F0.imprint","IMPRINT",FACE,{"disambiguationData":[TD([[makeQuery(id+"F0.imprint","IMPRINT",EDGE,{"derivedFrom":subQ1}),-1.0]])]});}
            var Q24;
            {var subQ1=sQuery(id+"F0.wireOp",EDGE,"E30.14.0");Q24=makeQuery(id+"F0.imprint","IMPRINT",FACE,{"disambiguationData":[TD([[makeQuery(id+"F0.imprint","IMPRINT",EDGE,{"derivedFrom":subQ1}),-1.0]])]});}
            var Q25;
            {var subQ1=sQuery(id+"F0.wireOp",EDGE,"E30.15.0");Q25=makeQuery(id+"F0.imprint","IMPRINT",FACE,{"disambiguationData":[TD([[makeQuery(id+"F0.imprint","IMPRINT",EDGE,{"derivedFrom":subQ1}),-1.0]])]});}
            var Q26;
            {var subQ1=sQuery(id+"F0.wireOp",EDGE,"E30.16.0");Q26=makeQuery(id+"F0.imprint","IMPRINT",FACE,{"disambiguationData":[TD([[makeQuery(id+"F0.imprint","IMPRINT",EDGE,{"derivedFrom":subQ1}),-1.0]])]});}
            var Q27;
            {var subQ0=sQuery(id+"F0.wireOp",EDGE,"E30.17.0");Q27=makeQuery(id+"F0.imprint","IMPRINT",FACE,{"disambiguationData":[TD([[makeQuery(id+"F0.imprint","IMPRINT",EDGE,{"derivedFrom":subQ0}),-1.0]])]});}
            var Q28;
            {var subQ1=sQuery(id+"F0.wireOp",EDGE,"E30.18.0");Q28=makeQuery(id+"F0.imprint","IMPRINT",FACE,{"disambiguationData":[TD([[makeQuery(id+"F0.imprint","IMPRINT",EDGE,{"derivedFrom":subQ1}),-1.0]])]});}
            var Q29;
            {var subQ1=sQuery(id+"F0.wireOp",EDGE,"E30.19.0");Q29=makeQuery(id+"F0.imprint","IMPRINT",FACE,{"disambiguationData":[TD([[makeQuery(id+"F0.imprint","IMPRINT",EDGE,{"derivedFrom":subQ1}),-1.0]])]});}
            var Q30;
            {var subQ1=sQuery(id+"F0.wireOp",EDGE,"E30.20.0");Q30=makeQuery(id+"F0.imprint","IMPRINT",FACE,{"disambiguationData":[TD([[makeQuery(id+"F0.imprint","IMPRINT",EDGE,{"derivedFrom":subQ1}),-1.0]])]});}
            var Q31;
            {var subQ1=sQuery(id+"F0.wireOp",EDGE,"E30.21.0");Q31=makeQuery(id+"F0.imprint","IMPRINT",FACE,{"disambiguationData":[TD([[makeQuery(id+"F0.imprint","IMPRINT",EDGE,{"derivedFrom":subQ1}),-1.0]])]});}
            var Q32;
            {var subQ0=sQuery(id+"F0.wireOp",EDGE,"E30.22.0");Q32=makeQuery(id+"F0.imprint","IMPRINT",FACE,{"disambiguationData":[TD([[makeQuery(id+"F0.imprint","IMPRINT",EDGE,{"derivedFrom":subQ0}),-1.0]])]});}
            var Q33;
            {var subQ0=sQuery(id+"F0.wireOp",EDGE,"E30.23.0");Q33=makeQuery(id+"F0.imprint","IMPRINT",FACE,{"disambiguationData":[TD([[makeQuery(id+"F0.imprint","IMPRINT",EDGE,{"derivedFrom":subQ0}),-1.0]])]});}
            var Q34;
            {var subQ1=sQuery(id+"F0.wireOp",EDGE,"E30.24.0");Q34=makeQuery(id+"F0.imprint","IMPRINT",FACE,{"disambiguationData":[TD([[makeQuery(id+"F0.imprint","IMPRINT",EDGE,{"derivedFrom":subQ1}),-1.0]])]});}
            var Q35;
            {var subQ1=sQuery(id+"F0.wireOp",EDGE,"E30.25.0");Q35=makeQuery(id+"F0.imprint","IMPRINT",FACE,{"disambiguationData":[TD([[makeQuery(id+"F0.imprint","IMPRINT",EDGE,{"derivedFrom":subQ1}),-1.0]])]});}
            var Q36;
            {var subQ1=sQuery(id+"F0.wireOp",EDGE,"E30.26.0");Q36=makeQuery(id+"F0.imprint","IMPRINT",FACE,{"disambiguationData":[TD([[makeQuery(id+"F0.imprint","IMPRINT",EDGE,{"derivedFrom":subQ1}),-1.0]])]});}
            var Q37;
            {var subQ1=sQuery(id+"F0.wireOp",EDGE,"E30.28.0");Q37=makeQuery(id+"F0.imprint","IMPRINT",FACE,{"disambiguationData":[TD([[makeQuery(id+"F0.imprint","IMPRINT",EDGE,{"derivedFrom":subQ1}),-1.0]])]});}
            var Q38;
            {var subQ1=sQuery(id+"F0.wireOp",EDGE,"E30.29.0");Q38=makeQuery(id+"F0.imprint","IMPRINT",FACE,{"disambiguationData":[TD([[makeQuery(id+"F0.imprint","IMPRINT",EDGE,{"derivedFrom":subQ1}),-1.0]])]});}
            var Q39;
            {var subQ0=sQuery(id+"F0.wireOp",EDGE,"E30.27.0");Q39=makeQuery(id+"F0.imprint","IMPRINT",FACE,{"disambiguationData":[TD([[makeQuery(id+"F0.imprint","IMPRINT",EDGE,{"derivedFrom":subQ0}),-1.0]])]});}
            extrude(context, id + "F3", {"entities" : qUnion([Q0, Q1, Q2, Q3, Q4, Q5, Q6, Q7, Q8, Q9, Q10, Q11, Q12, Q13, Q14, Q15, Q16, Q17, Q18, Q19, Q20, Q21, Q22, Q23, Q24, Q25, Q26, Q27, Q28, Q29, Q30, Q31, Q32, Q33, Q34, Q35, Q36, Q37, Q38, Q39]), "operationType" : NewBodyOperationType.ADD, "depth" : 4 * mm, "offsetDistance" : 25 * mm});
        }
    });
